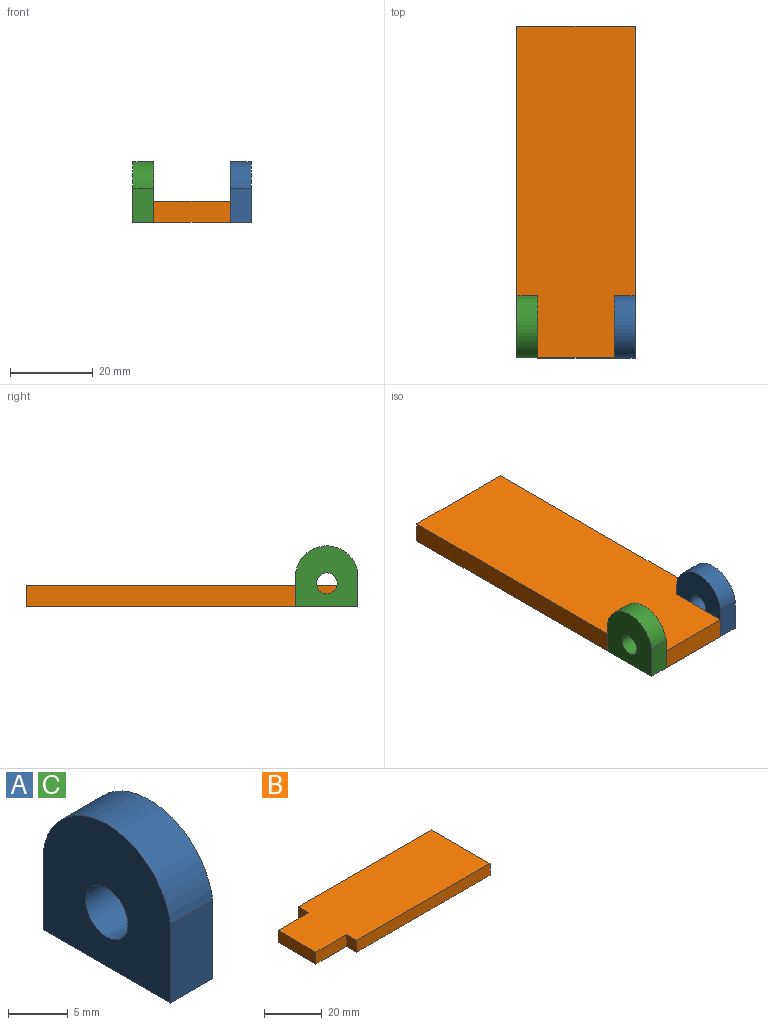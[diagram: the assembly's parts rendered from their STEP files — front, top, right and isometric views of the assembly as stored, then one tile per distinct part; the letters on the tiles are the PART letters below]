
ASSEMBLY  parts=3 mates=1
PART A: 7 faces, bbox 5x15x14.5 mm
  f0: plane 8x5mm, normal (0,-1,0), area 40mm2, adj f1,f4,f5,f6
  f1: plane 15x5mm, normal (0,0,-1), area 75mm2, adj f0,f2,f5,f6
  f2: plane 8x5mm, normal (0,1,0), area 40mm2, adj f1,f4,f5,f6
  f3: cylinder r=2.5mm len=5mm, axis (-1,0,0), area 78.5mm2, adj f5,f6
  f4: cylinder r=7.57mm len=15mm, axis (-1,0,0), area 108.5mm2, adj f0,f2,f5,f6
  f5: plane 15x14.53mm, normal (1,0,0), area 174.7mm2, adj f0,f1,f2,f3,f4
  f6: plane 15x14.53mm, normal (-1,0,0), area 174.7mm2, adj f0,f1,f2,f3,f4
PART B: 10 faces, bbox 80x28.5x5 mm
  f0: plane 65x5mm, normal (0,1,0), area 325mm2, adj f1,f7,f8,f9
  f1: plane 5x5mm, normal (-1,0,0), area 25mm2, adj f0,f2,f8,f9
  f2: plane 15x5mm, normal (0,1,0), area 75mm2, adj f1,f3,f8,f9
  f3: plane 18.5x5mm, normal (-1,0,0), area 92.5mm2, adj f2,f4,f8,f9
  f4: plane 15x5mm, normal (0,-1,0), area 75mm2, adj f3,f5,f8,f9
  f5: plane 5x5mm, normal (-1,0,0), area 25mm2, adj f4,f6,f8,f9
  f6: plane 65x5mm, normal (0,-1,0), area 325mm2, adj f5,f7,f8,f9
  f7: plane 28.5x5mm, normal (1,0,0), area 142.5mm2, adj f0,f6,f8,f9
  f8: plane 80x28.5mm, normal (0,0,1), area 2130mm2, adj f0,f1,f2,f3,f4,f5,f6,f7
  f9: plane 80x28.5mm, normal (0,0,-1), area 2130mm2, adj f0,f1,f2,f3,f4,f5,f6,f7
PART C: same geometry as A
PLACE A t=(-12.93,-7.64,-1.18)mm
PLACE B rot(axis=(0,0,1),90deg) t=(-22.18,24.86,-11.18)mm
PLACE C t=(-36.43,-7.64,-1.18)mm
MATE fastened B.f1 <-> C.f2  axis (0,-1,0) through (-33.93,-0.14,-11.18)mm
